# Revit family: magcardo_maxi_722212_003_67ac
name_source: partatom
category: Lighting Fixtures
units: mm (PartAtom-declared; Revit-internal decimal feet)

## family parameters
Cut with Voids When Loaded = No
Host = Face
Light Source = No
Part Type = Normal
Room Calculation Point = No
Round Connector Dimension = Use Diameter
Shared = No

## types (1)
- MAGCARDO maxi (1 x LED Modul 920 meat+, 1850 lm, 2000)
    Apparent Load = 33 VA
    Approval mark = CE
    CIE Flux Codes = 96 99 100 100 100
    Color Rendering = 90
    Color Temperature = 2000
    Default Elevation = 1800 mm
    Description = Series: MAGCARDO maxi
Projector unit for tool-free mounting in separate recessed frame. Luminaire top: die-cast aluminium, powder-coated. Rotation range 356° and swivel range ± 35°. Inner cover prevents view into the false ceiling. Black plastic ring and recessed LED to prevent glare from the side. Optical assembly with lens made of plastic (polycarbonate) for the best homogeneous light distribution - can be changed without tools. Special LED for illumination of meat included. Magnetic click locking mechanism for quick and convenient installation without tools: insert the recessed frame (1, 2 or 3-lamp) with clamp fastener (no tools required), push the luminaire head with the base plate into the recessed frame and fix magnetically. Including separate LED converter with connecting cable 600 mm.High quality converter without flickering and stroboscopic effect. Through-wiring box (5 pole) available as accessory. The following accessories can be mounted without use of tools: interchangeable lenses, honeycomb louvre, clear and frosted diffusers, white interchangeable plastic ring.Modular design: recessed mounting frame must be ordered separately! 
Colour: deep black, matt (RAL 9005)
Length: 172 mm
Width: 167 mm
Height: 137 mm
Recess height: 155 mm
Lamp: LED
Socket: without socket
Colour temperature: meat +
System power: 33 W
Rated luminous flux: 1850 lm
Luminous efficiency: 56 lm/W
Control gear: Regulated power supply
Protection class: II
Type of protection: IP 20
    Height = 0 mm  [stored 0 ft]
    Lamp = 1 x LED Modul 920 meat+
    Lamp Light Flux = 1850 lm
    Lamp count = 1
    Length = 172 mm
    Lifetime = 50000 h
    Luminous efficacy = 56 lm/W
    Manufacturer = RZB
    ModVariant = No
    Model = 722212.003
    Mounting Place = Ceiling, Wall
    Mounting Type = Recessed
    Number of Poles = 1
    OnlyDefault = Yes
    Power Factor = 1
    Product Name = MAGCARDO maxi
    Product group = Recessed projectors
    ProductGroupID = 401
    Protection Class = Protection class II
    Protection Degree = IP 20
    RLX_Detail_Level = 1
    RLX_Emergency_Light_Flux = 0 lm
    RLX_Emergency_Type = 0
    RLX_Emergency_Type_DB = No
    RlxData = <blob elided: 43341 chars, md5=781be017>
    Socket = socket
    Standby Power = 0 W
    System Light Flux = 1850 lm
    System Power = 33 W
    Type Comments = Product without accessories
    Type Image = 722048.003.jpg
    URL = http://relux.com
    VarID = ---
    Voltage = 230 V
    Voltage Range = 220-240 V
    Weight = 0.00 kg
    Width = 167 mm

note: [stored X ft] marks values corroborated as IEEE doubles in the binary element streams (Revit-internal decimal feet)

## geometry (parser evidence)
native form markers: Sweep x12
no freeform markers — native parametric forms only
